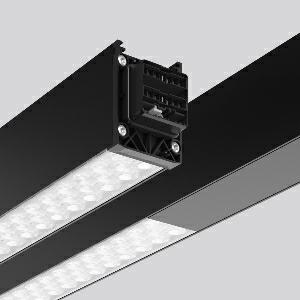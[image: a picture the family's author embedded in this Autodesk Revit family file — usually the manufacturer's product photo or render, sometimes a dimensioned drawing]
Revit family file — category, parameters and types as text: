
# Revit family: linedo_2_3m_90_1000_952390_833_476_703_b354
name_source: partatom
category: Lighting Fixtures
units: mm (PartAtom-declared; Revit-internal decimal feet)

## family parameters
Cut with Voids When Loaded = No
Host = Face
Light Source = No
Part Type = Normal
Room Calculation Point = No
Round Connector Dimension = Use Diameter
Shared = No

## types (1)
- LINEDO_2,3m_90_1000 (1 x LED Modul 830, 3900 lm, 3000)
    Apparent Load = 29 VA
    CIE Flux Codes = 73 96 99 100 100
    Color Rendering = 80
    Color Temperature = 3000
    Default Elevation = 1800 mm
    Description = LINEDO, 29 W, 3900 lm, 830, black, DALI
Continuous line luminaire, L 2291 B 58 H 76
    Height = 76 mm
    Lamp = 1 x LED Modul 830
    Lamp Light Flux = 3900 lm
    Lamp count = 1
    Length = 2291 mm
    Lifetime = 50000 h
    Luminous efficacy = 134 lm/W
    Manufacturer = RZB
    ModVariant = No
    Model = 952390.833.476.703
    Mounting Place = Ceiling
    Mounting Type = Surface mounted, Pendant
    Number of Poles = 1
    OnlyDefault = Yes
    Power Factor = 1
    Product Name = LINEDO_2,3m_90_1000
    Product group = Surface mounted continuous line luminaire system
    ProductGroupID = 310
    Protection Class = Protection class I
    Protection Degree = IP 54
    RLX_Detail_Level = 1
    RLX_Emergency_Light_Flux = 0 lm
    RLX_Emergency_Type = 0
    RLX_Emergency_Type_DB = No
    RlxData = <blob elided: 56549 chars, md5=3b54306b>
    Socket = socket
    Standby Power = 0 W
    System Light Flux = 3900 lm
    System Power = 29 W
    Type Comments = Product without accessories
    Type Image = 954590.853.476.504.jpg
    URL = http://relux.com
    VarID = ---
    Voltage = 230 V
    Voltage Range = 220-240 V
    Weight = 0.00 kg
    Width = 58 mm

## geometry (parser evidence)
native form markers: Blend x4, Sweep x12
no freeform markers — native parametric forms only
